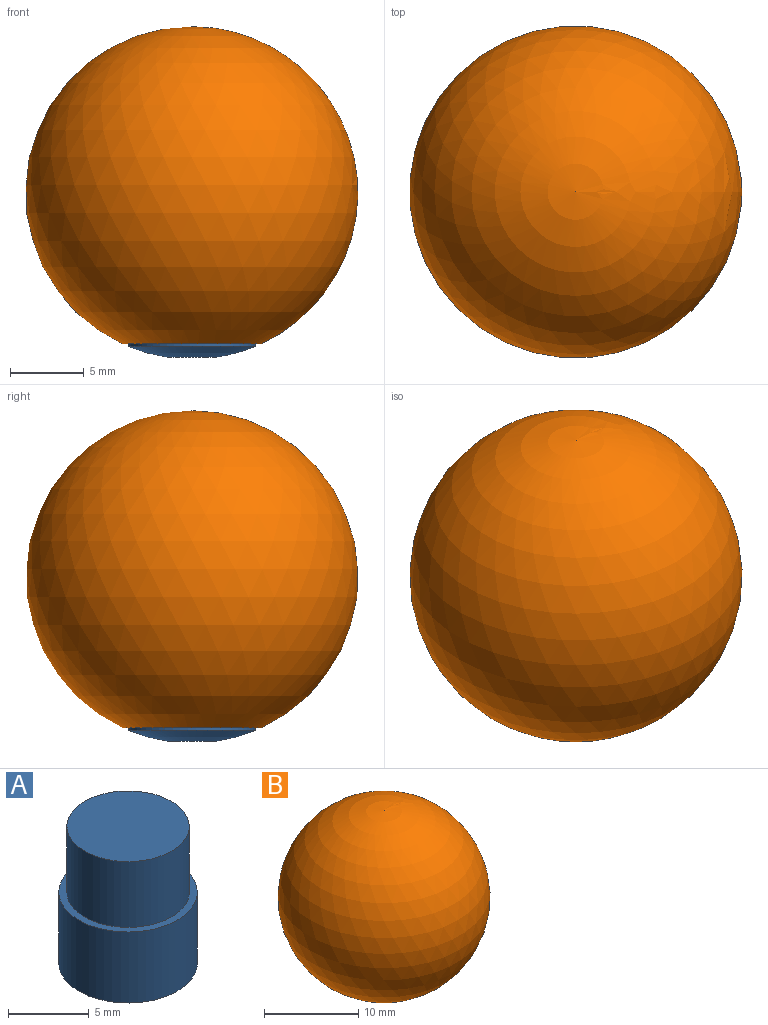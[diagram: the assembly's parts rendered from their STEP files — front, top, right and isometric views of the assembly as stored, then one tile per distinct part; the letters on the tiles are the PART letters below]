
ASSEMBLY  parts=2 mates=1
PART A: 7 faces, bbox 8.6x8.6x11.1 mm
  f0: cylinder r=1.59mm len=6mm, axis (0,0,1), area 59.8mm2, adj f1,f6
  f1: sphere r=11.25mm, area 52.4mm2, adj f0,f2
  f2: cylinder r=4.3mm len=8.6mm, axis (0,0,1), area 145.8mm2, adj f1,f3
  f3: plane 8.6x8.6mm, normal (0,0,1), area 12.7mm2, adj f2,f4
  f4: cylinder r=3.8mm len=7.6mm, axis (0,0,1), area 119.4mm2, adj f3,f5
  f5: plane 7.6x7.6mm, normal (0,0,1), area 45.4mm2, adj f4
  f6: plane 3.18x3.18mm, normal (0,0,-1), area 7.9mm2, adj f0
PART B: 5 faces, bbox 22.5x22.5x21.5 mm
  f0: cylinder r=4.7mm len=9.4mm, axis (0,0,1), area 154.2mm2, adj f1,f4
  f1: sphere r=11.25mm, area 1517.7mm2, adj f0
  f2: sphere r=4.2mm, area 110.8mm2, adj f3
  f3: cylinder r=4.2mm len=8.4mm, axis (0,0,1), area 131.9mm2, adj f2,f4
  f4: plane 9.4x9.4mm, normal (0,0,-1), area 14mm2, adj f0,f3
PLACE A t=(3.49,-4.1,1.33)mm
PLACE B t=(3.49,-4.1,10.73)mm
MATE fastened B.f0 <-> A.f0  axis (0,0,-1) through (3.49,-4.1,5.73)mm
